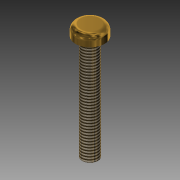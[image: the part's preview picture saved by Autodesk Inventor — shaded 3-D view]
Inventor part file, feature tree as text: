
AUTODESK INVENTOR PART (.ipt)
format: ipt  version: 2015 (Build 190159000, 159)  size: 111,616 bytes
history: native  units: mm
features: extrude x2, sketch x2, other x1, fillet x1, thread x1
ambient origin geometry x8: Origin, YZ Plane, XZ Plane, XY Plane, X Axis, Y Axis, Z Axis, Center Point
bodies: Body1 (feature_tree)
feature tree (7):
  other  "ソリッド1"
  extrude  "押し出し1"  Depth=5.5mm
  fillet  "フィレット1"  Radius=2.0mm
  extrude  "押し出し2"  Depth=1.0mm
  thread  "ねじ1"
  sketch  "スケッチ1"
  sketch  "スケッチ2"
